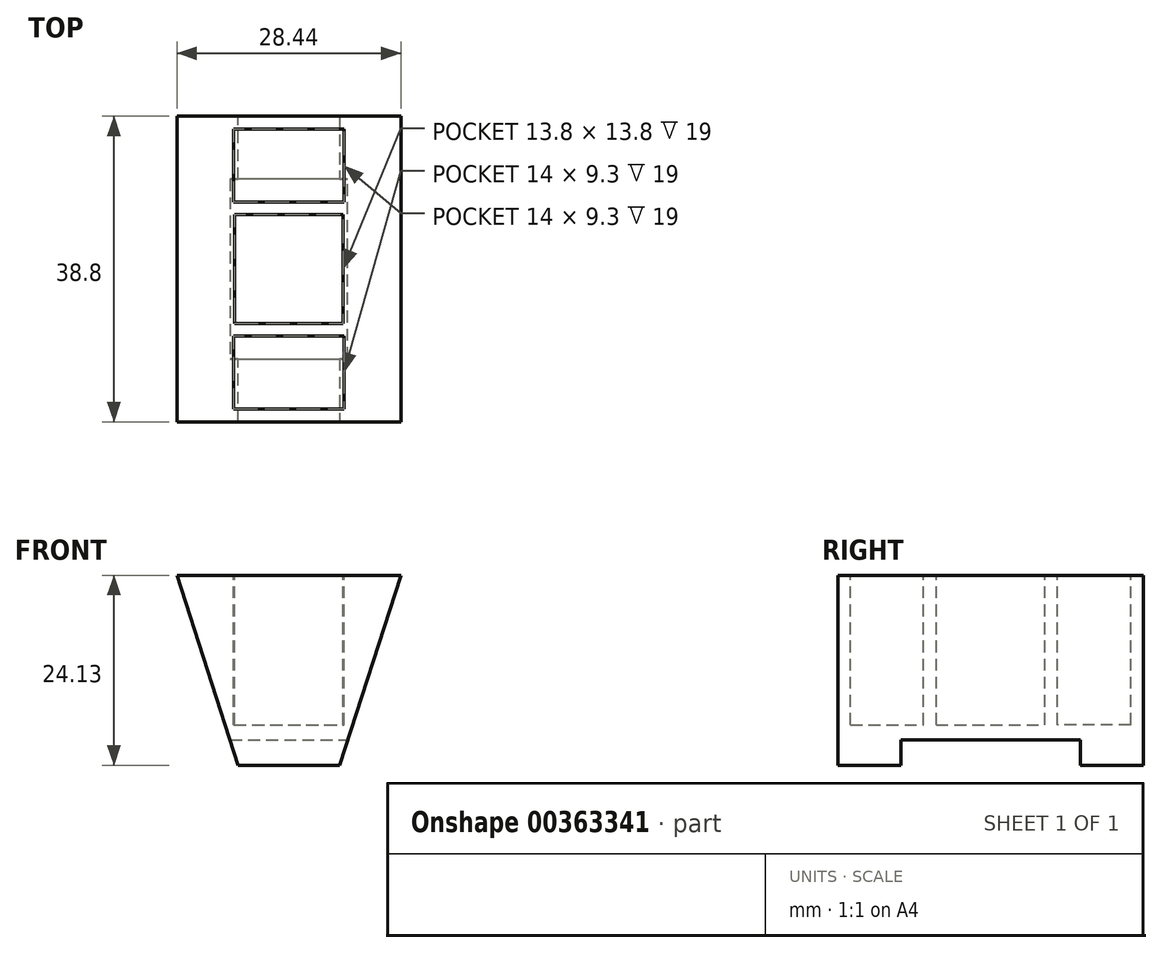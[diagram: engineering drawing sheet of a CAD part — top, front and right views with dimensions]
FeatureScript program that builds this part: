
annotation { "Feature Type Name" : "Feature", "Feature Type Description" : "" }
export const myFeature = defineFeature(function(context is Context, id is Id, definition is map)
    precondition{}
    {
        {
            var Q0;
            Q0=qCreatedBy(makeId("Top.planeOp"),FACE);
            cPlane(context, id + "F0", {"entities" : qUnion([Q0]), "cplaneType" : CPlaneType.OFFSET, "offset" : 36.12 * mm, "width" : 150 * mm, "height" : 150 * mm});
        }
        {
            var Q0;
            Q0=qCreatedBy(id+"F0.planeOp",FACE);
            var sketch = newSketch(context, id + "F1", { "sketchPlane" : qUnion([Q0])});
            skLineSegment(sketch, "E0", {"start": v(-18.1, 0) * mm, "end": v(-18.1, -38.8) * mm});
            skLineSegment(sketch, "E1", {"start": v(-18.1, -38.8) * mm, "end": v(18.1, -38.8) * mm});
            skLineSegment(sketch, "E2", {"start": v(18.1, -38.8) * mm, "end": v(18.1, 0) * mm});
            skLineSegment(sketch, "E3", {"start": v(-18.1, 0) * mm, "end": v(18.1, 0) * mm});
            skSolve(sketch);
        }
        {
            var Q0;
            Q0=qCreatedBy(makeId("Top.planeOp"),FACE);
            var sketch = newSketch(context, id + "F2", { "sketchPlane" : qUnion([Q0])});
            skLineSegment(sketch, "E4", {"start": v(6.43, 0) * mm, "end": v(6.43, -38.8) * mm});
            skLineSegment(sketch, "E5", {"start": v(6.43, -38.8) * mm, "end": v(-6.43, -38.8) * mm});
            skLineSegment(sketch, "E6", {"start": v(-6.43, -38.8) * mm, "end": v(-6.43, 0) * mm});
            skLineSegment(sketch, "E7", {"start": v(-6.43, 0) * mm, "end": v(6.43, 0) * mm});
            skSolve(sketch);
        }
        {
            var Q0;
            Q0=makeQuery(id+"F1.imprint","IMPRINT",FACE,{"disambiguationData":[TD([[makeQuery(id+"F1.imprint","IMPRINT",EDGE,{"derivedFrom":sQuery(id+"F1.wireOp",EDGE,"E0")}),1.0]])]});
            var Q1;
            Q1=makeQuery(id+"F2.imprint","IMPRINT",FACE,{"disambiguationData":[TD([[makeQuery(id+"F2.imprint","IMPRINT",EDGE,{"derivedFrom":sQuery(id+"F2.wireOp",EDGE,"E4")}),-1.0]])]});
            loft(context, id + "F3", {"sheetProfilesArray" : [{ "sheetProfileEntities" : qUnion([Q0]) }, { "sheetProfileEntities" : qUnion([Q1]) }]});
        }
        {
            var Q0;
            Q0=makeQuery(id+"F3.opLoft","CAP_FACE",FACE,{"disambiguationData":[OSD([makeQuery(id+"F1.imprint","IMPRINT",FACE,{"disambiguationData":[TD([[makeQuery(id+"F1.imprint","IMPRINT",EDGE,{"derivedFrom":sQuery(id+"F1.wireOp",EDGE,"E0")}),1.0]])]})])],"isStart":true});
            extrude(context, id + "F4", {"entities" : qUnion([Q0]), "operationType" : NewBodyOperationType.REMOVE, "oppositeDirection" : true, "depth" : 12 * mm});
        }
        {
            var Q0;
            Q0=qCreatedBy(id+"F0.planeOp",FACE);
            var sketch = newSketch(context, id + "F5", { "sketchPlane" : qUnion([Q0])});
            skLineSegment(sketch, "E8", {"start": v(-6.9, -12.5) * mm, "end": v(6.9, -12.5) * mm});
            skLineSegment(sketch, "E9", {"start": v(6.9, -12.5) * mm, "end": v(6.9, -26.3) * mm});
            skLineSegment(sketch, "E10", {"start": v(6.9, -26.3) * mm, "end": v(-6.9, -26.3) * mm});
            skLineSegment(sketch, "E11", {"start": v(-6.9, -26.3) * mm, "end": v(-6.9, -12.5) * mm});
            skSolve(sketch);
        }
        {
            var Q0;
            Q0=makeQuery(id+"F5.imprint","IMPRINT",FACE,{"disambiguationData":[TD([[makeQuery(id+"F5.imprint","IMPRINT",EDGE,{"derivedFrom":sQuery(id+"F5.wireOp",EDGE,"E8")}),-1.0]])]});
            extrude(context, id + "F6", {"entities" : qUnion([Q0]), "operationType" : NewBodyOperationType.REMOVE, "oppositeDirection" : true, "depth" : 31 * mm});
        }
        {
            var Q0;
            Q0=qCreatedBy(makeId("Top.planeOp"),FACE);
            var sketch = newSketch(context, id + "F7", { "sketchPlane" : qUnion([Q0])});
            skLineSegment(sketch, "E12", {"start": v(-10, -30.8) * mm, "end": v(10, -30.8) * mm});
            skLineSegment(sketch, "E13", {"start": v(10, -30.8) * mm, "end": v(10, -8) * mm});
            skLineSegment(sketch, "E14", {"start": v(10, -8) * mm, "end": v(-10, -8) * mm});
            skLineSegment(sketch, "E15", {"start": v(-10, -8) * mm, "end": v(-10, -30.8) * mm});
            skSolve(sketch);
        }
        {
            var Q0;
            Q0=qSketchRegion(id+"F7",true);
            extrude(context, id + "F8", {"entities" : qUnion([Q0]), "operationType" : NewBodyOperationType.REMOVE, "depth" : 3.2 * mm});
        }
        {
            var Q0;
            Q0=qCreatedBy(id+"F0.planeOp",FACE);
            var sketch = newSketch(context, id + "F9", { "sketchPlane" : qUnion([Q0])});
            skLineSegment(sketch, "E16", {"start": v(-7, -10.9) * mm, "end": v(7, -10.9) * mm});
            skLineSegment(sketch, "E17", {"start": v(7, -10.9) * mm, "end": v(7, -1.6) * mm});
            skLineSegment(sketch, "E18", {"start": v(7, -1.6) * mm, "end": v(-7, -1.6) * mm});
            skLineSegment(sketch, "E19", {"start": v(-7, -1.6) * mm, "end": v(-7, -10.9) * mm});
            skLineSegment(sketch, "E20", {"start": v(-19.21, -19.4) * mm, "end": v(16.55, -19.4) * mm, "construction": true});
            skLineSegment(sketch, "E21.MirrorCS", {"start": v(-7, -27.9) * mm, "end": v(7, -27.9) * mm});
            skLineSegment(sketch, "E22.MirrorCS", {"start": v(-7, -37.2) * mm, "end": v(-7, -27.9) * mm});
            skLineSegment(sketch, "E23.MirrorCS", {"start": v(7, -27.9) * mm, "end": v(7, -37.2) * mm});
            skLineSegment(sketch, "E24.MirrorCS", {"start": v(7, -37.2) * mm, "end": v(-7, -37.2) * mm});
            skSolve(sketch);
        }
        {
            var Q0;
            Q0=qSketchRegion(id+"F9",true);
            extrude(context, id + "F10", {"entities" : qUnion([Q0]), "operationType" : NewBodyOperationType.REMOVE, "oppositeDirection" : true, "depth" : 31 * mm});
        }
    });
